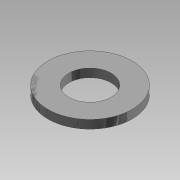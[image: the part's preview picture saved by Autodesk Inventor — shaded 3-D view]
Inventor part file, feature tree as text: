
AUTODESK INVENTOR PART (.ipt)
format: ipt  version: 2013 SP2 (Build 170200200, 200)  size: 76,288 bytes
history: native  units: mm
features: extrude x1, sketch x1
ambient origin geometry x8: Origin, YZ Plane, XZ Plane, XY Plane, X Axis, Y Axis, Z Axis, Center Point
bodies: Solid1 (feature_tree)
feature tree (2):
  extrude  "Extrusion1"  Depth=10.0mm
  sketch  "Sketch1"  dims[d0=5.0mm d1=10.0mm d2=1.0mm d3=0.0mm]
